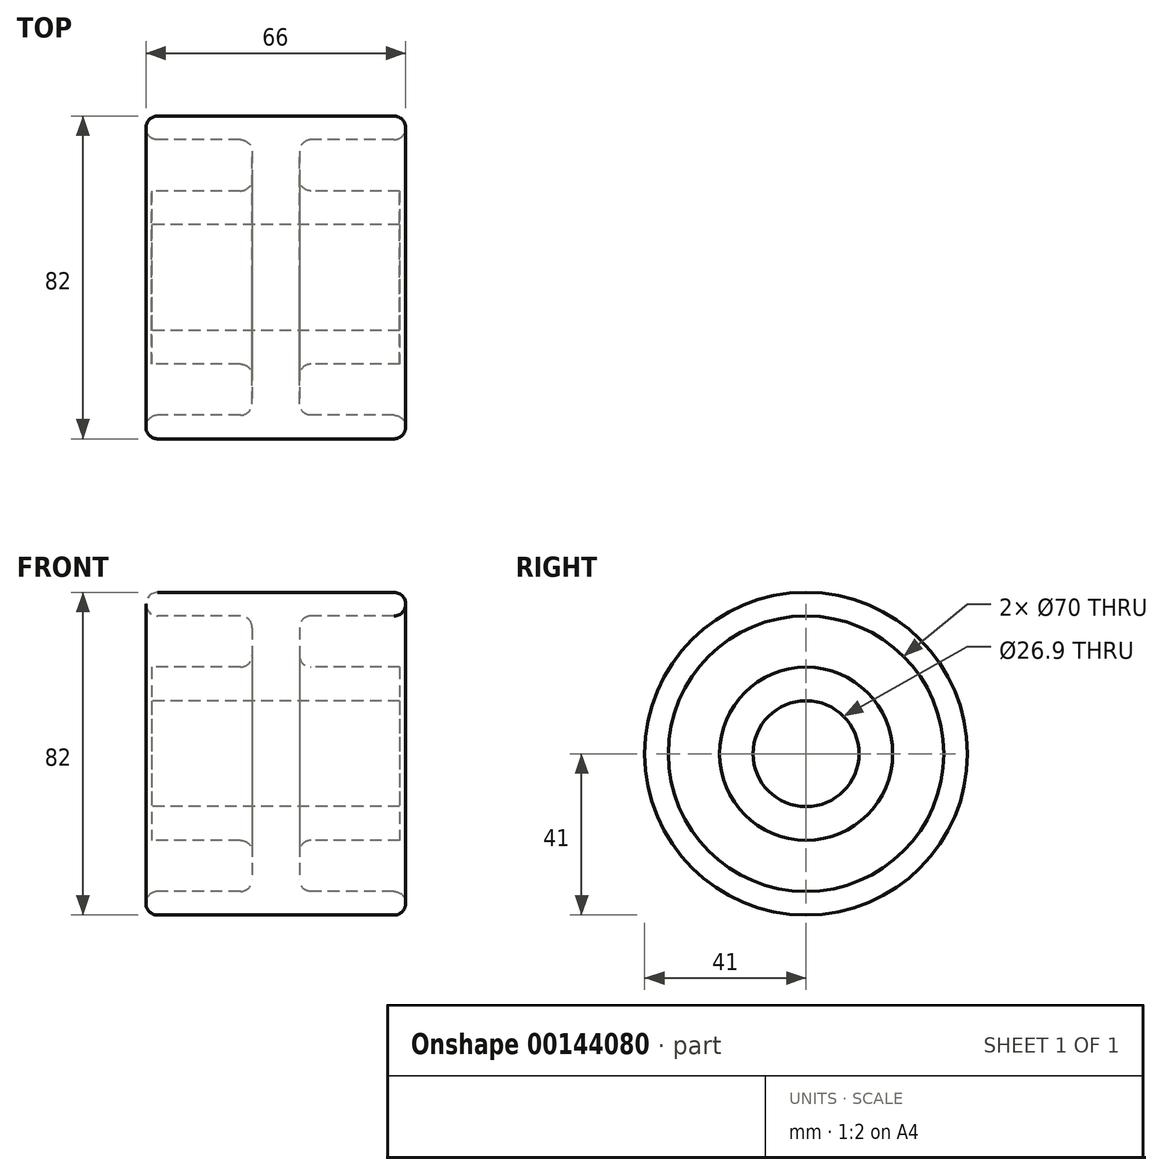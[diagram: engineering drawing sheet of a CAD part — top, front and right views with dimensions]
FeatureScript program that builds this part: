
annotation { "Feature Type Name" : "Feature", "Feature Type Description" : "" }
export const myFeature = defineFeature(function(context is Context, id is Id, definition is map)
    precondition{}
    {
        {
            var Q0;
            Q0=qCreatedBy(makeId("Front.planeOp"),FACE);
            var sketch = newSketch(context, id + "F0", { "sketchPlane" : qUnion([Q0])});
            skLineSegment(sketch, "E0", {"start": v(31.5, 0) * mm, "end": v(31.5, 8.55) * mm});
            skLineSegment(sketch, "E1", {"start": v(31.5, 8.55) * mm, "end": v(9, 8.55) * mm});
            skLineSegment(sketch, "E2", {"start": v(9, 21.55) * mm, "end": v(30, 21.55) * mm});
            skLineSegment(sketch, "E3", {"start": v(30, 27.55) * mm, "end": v(-30, 27.55) * mm});
            skLineSegment(sketch, "E4", {"start": v(-31.5, 0) * mm, "end": v(-31.5, 8.55) * mm});
            skLineSegment(sketch, "E5", {"start": v(-31.5, 8.55) * mm, "end": v(-9, 8.55) * mm});
            skLineSegment(sketch, "E6", {"start": v(-9, 21.55) * mm, "end": v(-30, 21.55) * mm});
            skArc(sketch, "E7", {"start": v(-30, 27.55) * mm, "mid": v(-33, 24.55) * mm, "end": v(-30, 21.55) * mm});
            skArc(sketch, "E8", {"start": v(30, 21.55) * mm, "mid": v(33, 24.55) * mm, "end": v(30, 27.55) * mm});
            skLineSegment(sketch, "E9", {"start": v(-31.5, 0) * mm, "end": v(31.5, 0) * mm});
            skLineSegment(sketch, "E10", {"start": v(-25, -13.45) * mm, "end": v(65.42, -13.45) * mm, "construction": true});
            skLineSegment(sketch, "E11", {"start": v(-6, 11.55) * mm, "end": v(-6, 18.55) * mm});
            skLineSegment(sketch, "E12", {"start": v(6, 11.55) * mm, "end": v(6, 18.55) * mm});
            skArc(sketch, "E13", {"start": v(-9, 8.55) * mm, "mid": v(-6.88, 9.43) * mm, "end": v(-6, 11.55) * mm});
            skArc(sketch, "E14", {"start": v(6, 11.55) * mm, "mid": v(6.88, 9.43) * mm, "end": v(9, 8.55) * mm});
            skArc(sketch, "E15", {"start": v(-6, 18.55) * mm, "mid": v(-6.88, 20.67) * mm, "end": v(-9, 21.55) * mm});
            skLineSegment(sketch, "E16", {"start": v(0, 0) * mm, "end": v(0, 27.55) * mm, "construction": true});
            skArc(sketch, "E17", {"start": v(9, 21.55) * mm, "mid": v(6.88, 20.67) * mm, "end": v(6, 18.55) * mm});
            skSolve(sketch);
        }
        {
            var Q0;
            Q0=makeQuery(id+"F0.imprint","IMPRINT",FACE,{"disambiguationData":[TD([[makeQuery(id+"F0.imprint","IMPRINT",EDGE,{"derivedFrom":sQuery(id+"F0.wireOp",EDGE,"E0")}),1.0]])]});
            var Q1;
            Q1=sQuery(id+"F0.wireOp",EDGE,"E10");
            revolve(context, id + "F1", {"entities" : qUnion([Q0]), "axis" : qUnion([Q1]), "revolveType" : RevolveType.FULL});
        }
    });
